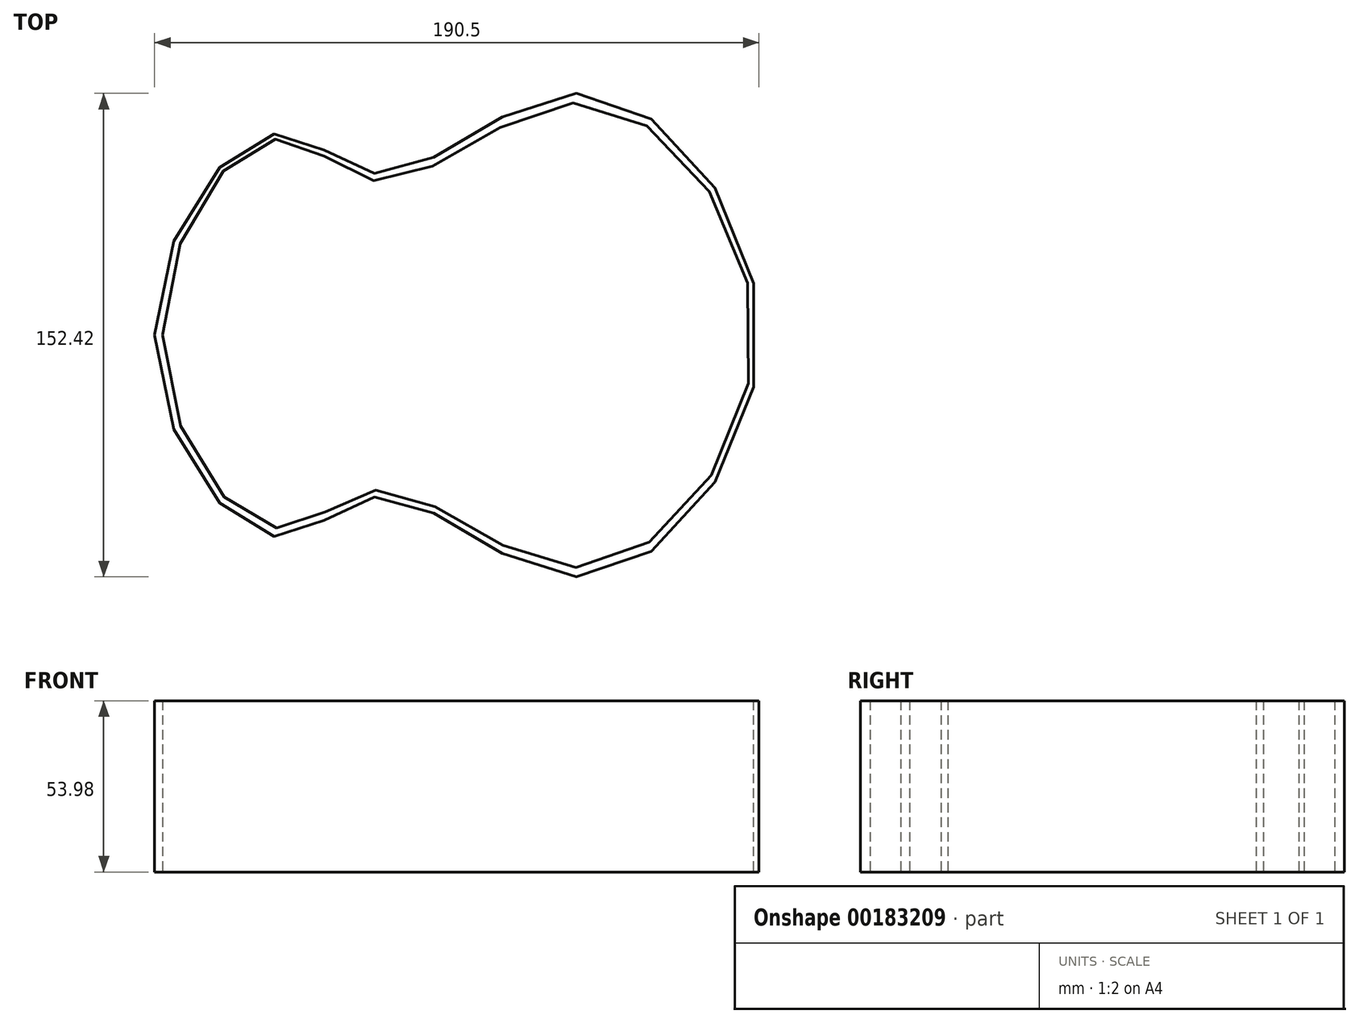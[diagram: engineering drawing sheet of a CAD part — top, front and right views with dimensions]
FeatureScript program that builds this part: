
annotation { "Feature Type Name" : "Feature", "Feature Type Description" : "" }
export const myFeature = defineFeature(function(context is Context, id is Id, definition is map)
    precondition{}
    {
        {
            var Q0;
            Q0=qCreatedBy(makeId("Top.planeOp"),FACE);
            var sketch = newSketch(context, id + "F0", { "sketchPlane" : qUnion([Q0])});
            skLineSegment(sketch, "E0", {"start": v(-157.48, -34.63) * mm, "end": v(33.02, -34.63) * mm, "construction": true});
            skLineSegment(sketch, "E1", {"start": v(-23.09, -34.63) * mm, "end": v(-23.09, 41.57) * mm, "construction": true});
            skLineSegment(sketch, "E2", {"start": v(-23.09, -34.63) * mm, "end": v(-23.09, -110.83) * mm, "construction": true});
            skLineSegment(sketch, "E3", {"start": v(-85.45, -34.63) * mm, "end": v(-85.45, 16.17) * mm, "construction": true});
            skLineSegment(sketch, "E4", {"start": v(-85.45, -34.63) * mm, "end": v(-85.45, -85.43) * mm, "construction": true});
            skLineSegment(sketch, "E5", {"start": v(-119.02, -34.63) * mm, "end": v(-119.02, 28.87) * mm, "construction": true});
            skLineSegment(sketch, "E6", {"start": v(-119.02, -34.63) * mm, "end": v(-119.02, -98.13) * mm, "construction": true});
            skFitSpline(sketch, "E7", {"points": [v(-157.48, -34.63) * mm, v(-119.02, 28.87) * mm, v(-85.45, 16.17) * mm, v(-23.09, 41.57) * mm, v(33.02, -34.63) * mm, v(-23.09, -110.83) * mm, v(-85.45, -85.43) * mm, v(-119.02, -98.13) * mm, v(-157.48, -34.63) * mm]});
            skLineSegment(sketch, "E8", {"start": v(-119.02, -34.63) * mm, "end": v(-155, -34.63) * mm, "construction": true});
            skLineSegment(sketch, "E9", {"start": v(-119.02, -34.63) * mm, "end": v(-119.02, 27.2) * mm, "construction": true});
            skLineSegment(sketch, "E10", {"start": v(-85.45, -34.63) * mm, "end": v(-85.45, 13.79) * mm, "construction": true});
            skLineSegment(sketch, "E11", {"start": v(-85.45, 13.79) * mm, "end": v(-85.45, -83.4) * mm, "construction": true});
            skLineSegment(sketch, "E12", {"start": v(-85.45, -83.4) * mm, "end": v(-85.45, -34.63) * mm, "construction": true});
            skLineSegment(sketch, "E13", {"start": v(-119.02, -34.63) * mm, "end": v(-119.02, -95.39) * mm, "construction": true});
            skLineSegment(sketch, "E14", {"start": v(-119.02, -95.39) * mm, "end": v(-119.02, -34.63) * mm, "construction": true});
            skLineSegment(sketch, "E15", {"start": v(-23.09, -34.63) * mm, "end": v(-23.09, -107.8) * mm, "construction": true});
            skLineSegment(sketch, "E16", {"start": v(-23.09, -107.8) * mm, "end": v(-23.09, 38.59) * mm, "construction": true});
            skLineSegment(sketch, "E17", {"start": v(-23.09, 38.59) * mm, "end": v(-23.09, -34.63) * mm, "construction": true});
            skLineSegment(sketch, "E18", {"start": v(-23.09, -34.63) * mm, "end": v(31.23, -34.63) * mm, "construction": true});
            skLineSegment(sketch, "E19", {"start": v(31.23, -34.63) * mm, "end": v(-23.09, -34.63) * mm, "construction": true});
            skFitSpline(sketch, "E20", {"points": [v(-155, -34.63) * mm, v(-119.02, 27.2) * mm, v(-85.45, 13.79) * mm, v(-23.09, 38.59) * mm, v(31.23, -34.63) * mm, v(-23.09, -107.8) * mm, v(-85.45, -83.4) * mm, v(-119.02, -95.39) * mm, v(-155, -34.63) * mm]});
            skSolve(sketch);
        }
        {
            var Q0;
            Q0=makeQuery(id+"F0.imprint","IMPRINT",FACE,{"disambiguationData":[TD([[makeQuery(id+"F0.imprint","IMPRINT",EDGE,{"derivedFrom":sQuery(id+"F0.wireOp",EDGE,"E7")}),-1.0]])]});
            extrude(context, id + "F1", {"entities" : qUnion([Q0]), "depth" : 53.97 * mm});
        }
    });
